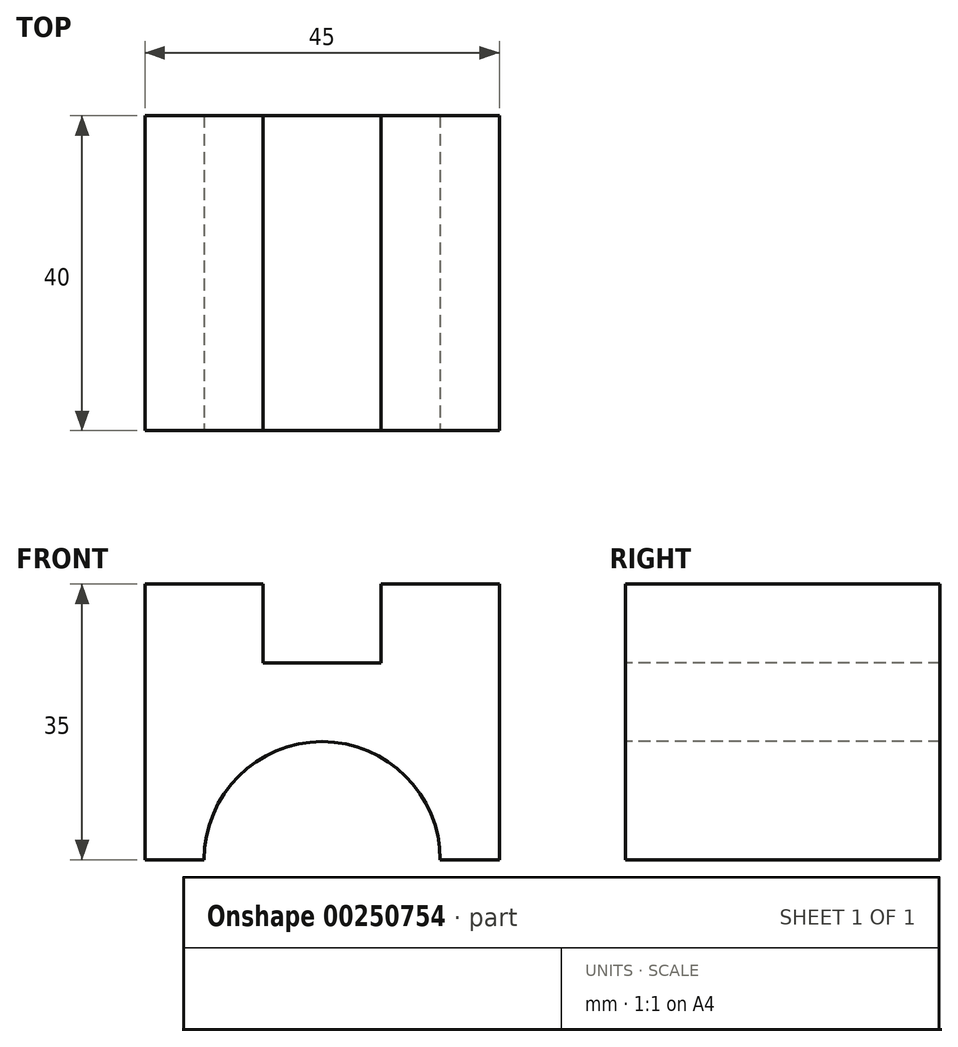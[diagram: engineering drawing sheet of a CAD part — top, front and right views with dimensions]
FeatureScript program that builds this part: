
annotation { "Feature Type Name" : "Feature", "Feature Type Description" : "" }
export const myFeature = defineFeature(function(context is Context, id is Id, definition is map)
    precondition{}
    {
        {
            var Q0;
            Q0=qCreatedBy(makeId("Top.planeOp"),FACE);
            var sketch = newSketch(context, id + "F0", { "sketchPlane" : qUnion([Q0])});
            skLineSegment(sketch, "E0", {"start": v(-26.92, -28.38) * mm, "end": v(18.08, -28.38) * mm});
            skLineSegment(sketch, "E1", {"start": v(18.08, -28.38) * mm, "end": v(18.08, 11.62) * mm});
            skLineSegment(sketch, "E2", {"start": v(18.08, 11.62) * mm, "end": v(-26.92, 11.62) * mm});
            skLineSegment(sketch, "E3", {"start": v(-26.92, 11.62) * mm, "end": v(-26.92, -28.38) * mm});
            skSolve(sketch);
        }
        {
            var Q0;
            Q0=makeQuery(id+"F0.imprint","IMPRINT",FACE,{"disambiguationData":[TD([[makeQuery(id+"F0.imprint","IMPRINT",EDGE,{"derivedFrom":sQuery(id+"F0.wireOp",EDGE,"E0")}),1.0]])]});
            extrude(context, id + "F1", {"entities" : qUnion([Q0]), "depth" : 25 * mm});
        }
        {
            var Q0;
            Q0=makeQuery(id+"F1.opExtrude","CAP_FACE",FACE,{"disambiguationData":[OSD([sQuery(id+"F0.wireOp",EDGE,"E0"),sQuery(id+"F0.wireOp",EDGE,"E1"),sQuery(id+"F0.wireOp",EDGE,"E2"),sQuery(id+"F0.wireOp",EDGE,"E3")])],"isStart":false});
            var sketch = newSketch(context, id + "F2", { "sketchPlane" : qUnion([Q0])});
            skLineSegment(sketch, "E4", {"start": v(3.08, 11.62) * mm, "end": v(3.08, -28.38) * mm});
            skLineSegment(sketch, "E5", {"start": v(-11.92, 11.62) * mm, "end": v(-11.92, -28.38) * mm});
            skSolve(sketch);
        }
        {
            var Q0;
            Q0 = qSketchRegion(id + "F2", true);
            var Q1;
            {var subQ0=sQuery(id+"F2.wireOp",EDGE,"E4");Q1=makeQuery(id+"F2.imprint","IMPRINT",FACE,{"disambiguationData":[TD([[makeQuery(id+"F2.imprint","IMPRINT",EDGE,{"derivedFrom":subQ0}),1.0]])]});}
            var Q2;
            {var subQ0=sQuery(id+"F2.wireOp",EDGE,"E5");Q2=makeQuery(id+"F2.imprint","IMPRINT",FACE,{"disambiguationData":[TD([[makeQuery(id+"F2.imprint","IMPRINT",EDGE,{"derivedFrom":subQ0}),-1.0]])]});}
            extrude(context, id + "F3", {"entities" : qUnion([Q0, Q1, Q2]), "operationType" : NewBodyOperationType.ADD, "depth" : 10 * mm});
        }
        {
            var Q0;
            {var subQ0=sQuery(id+"F0.wireOp",EDGE,"E0");var subQ1=makeQuery(id+"F1.opExtrude","CAP_EDGE",EDGE,{"disambiguationData":[OSD([subQ0])],"isStart":false});Q0=makeQuery(id+"F3.boolean.opBoolean","MERGE",FACE,{"derivedFrom":[makeQuery(id+"F1.opExtrude","SWEPT_FACE",FACE,{"disambiguationData":[OSD([subQ0])]}),makeQuery(id+"F3.opExtrude","SWEPT_FACE",FACE,{"disambiguationData":[OSD([subQ0]),TDD([makeQuery(id+"F2.imprint","IMPRINT",EDGE,{"disambiguationData":[TD([[makeQuery(id+"F2.imprint","INTERSECT",VERTEX,{"derivedFrom":[subQ1,makeQuery(id+"F1.opExtrude","CAP_EDGE",EDGE,{"disambiguationData":[OSD([sQuery(id+"F0.wireOp",EDGE,"E3")])],"isStart":false})]}),-1.0]])],"derivedFrom":subQ1})])]}),makeQuery(id+"F3.opExtrude","SWEPT_FACE",FACE,{"disambiguationData":[OSD([subQ0]),TDD([makeQuery(id+"F2.imprint","IMPRINT",EDGE,{"disambiguationData":[TD([[makeQuery(id+"F2.imprint","INTERSECT",VERTEX,{"derivedFrom":[subQ1,makeQuery(id+"F1.opExtrude","CAP_EDGE",EDGE,{"disambiguationData":[OSD([sQuery(id+"F0.wireOp",EDGE,"E1")])],"isStart":false})]}),1.0]])],"derivedFrom":subQ1})])]})]});}
            var sketch = newSketch(context, id + "F4", { "sketchPlane" : qUnion([Q0])});
            skArc(sketch, "E6", {"start": v(10.58, 0) * mm, "mid": v(-4.42, 15) * mm, "end": v(-19.42, 0) * mm});
            skLineSegment(sketch, "E7.0", {"start": v(-26.92, 0) * mm, "end": v(18.08, 0) * mm});
            skSolve(sketch);
        }
        {
            var Q0;
            Q0 = qSketchRegion(id + "F4", true);
            extrude(context, id + "F5", {"entities" : qUnion([Q0]), "operationType" : NewBodyOperationType.REMOVE, "endBound" : BoundingType.THROUGH_ALL, "oppositeDirection" : true, "depth" : 25.4 * mm});
        }
    });
